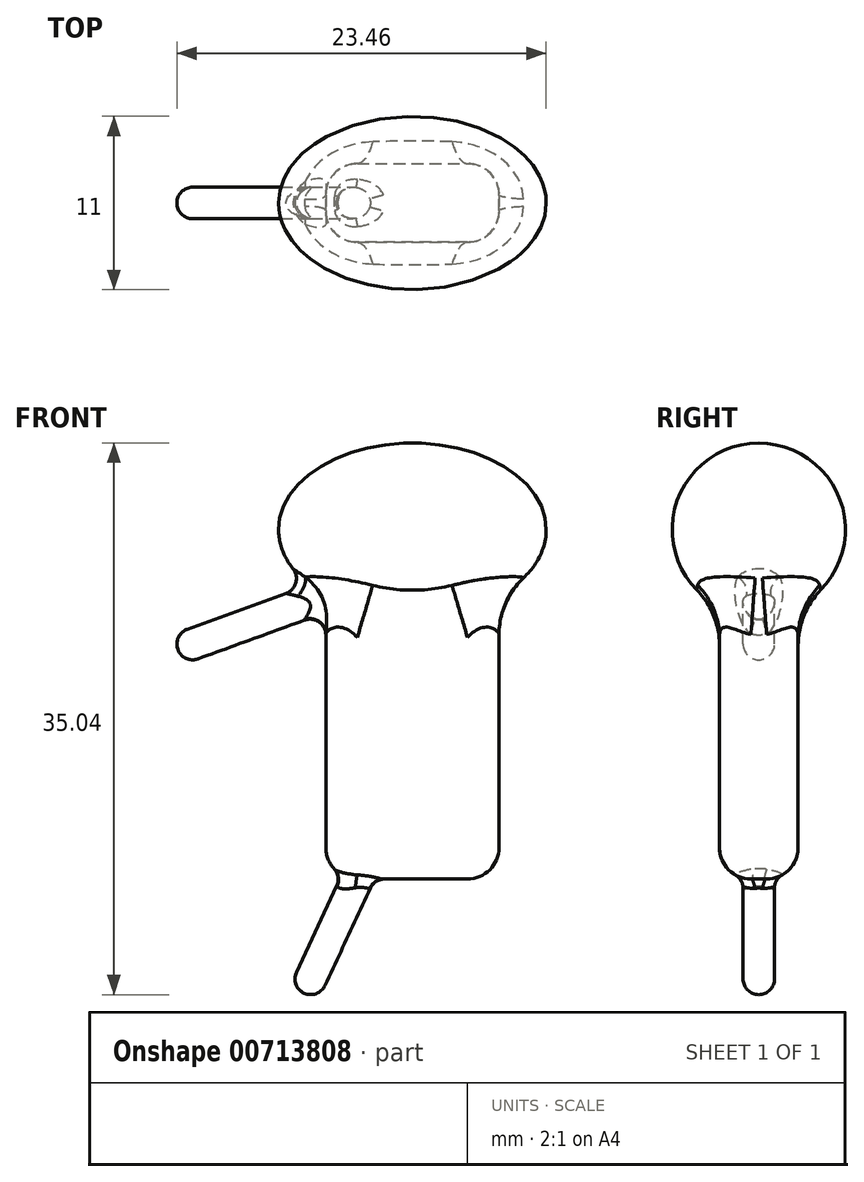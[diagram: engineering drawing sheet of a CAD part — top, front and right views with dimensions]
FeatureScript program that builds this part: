
annotation { "Feature Type Name" : "Feature", "Feature Type Description" : "" }
export const myFeature = defineFeature(function(context is Context, id is Id, definition is map)
    precondition{}
    {
        {
            var Q0;
            Q0=qCreatedBy(makeId("Front.planeOp"),FACE);
            var sketch = newSketch(context, id + "F0", { "sketchPlane" : qUnion([Q0])});
            skLineSegment(sketch, "E0", {"start": v(-29.63, 35) * mm, "end": v(21.78, 35) * mm, "construction": true});
            skEllipse(sketch, "E1", {"center": v(0, 29.5) * mm, "majorRadius": 8.5 * mm, "minorRadius": 5.5 * mm, "majorAxis": v(1, 0)});
            skLineSegment(sketch, "E2.bottom", {"start": v(-5.5, 7.3) * mm, "end": v(5.5, 7.3) * mm});
            skLineSegment(sketch, "E2.top", {"start": v(-5.5, 25.3) * mm, "end": v(5.5, 25.3) * mm});
            skLineSegment(sketch, "E2.left", {"start": v(-5.5, 7.3) * mm, "end": v(-5.5, 25.3) * mm});
            skLineSegment(sketch, "E2.right", {"start": v(5.5, 7.3) * mm, "end": v(5.5, 25.3) * mm});
            skLineSegment(sketch, "E3", {"start": v(-5.5, 25.3) * mm, "end": v(-14.9, 21.89) * mm});
            skLineSegment(sketch, "E4", {"start": v(-3.5, 7.3) * mm, "end": v(-6.9, 0) * mm});
            skLineSegment(sketch, "E5.MirrorCS", {"start": v(5.5, 25.3) * mm, "end": v(14.9, 21.89) * mm});
            skLineSegment(sketch, "E6.MirrorCS", {"start": v(3.5, 7.3) * mm, "end": v(6.9, 0) * mm});
            skLineSegment(sketch, "E7", {"start": v(-8.5, 29.5) * mm, "end": v(8.5, 29.5) * mm});
            skSolve(sketch);
        }
        {
            var Q0;
            {var subQ0=sQuery(id+"F0.wireOp",EDGE,"E7");Q0=makeQuery(id+"F0.imprint","IMPRINT",FACE,{"disambiguationData":[TD([[makeQuery(id+"F0.imprint","IMPRINT",EDGE,{"derivedFrom":subQ0}),1.0]])]});}
            var Q1;
            Q1=sQuery(id+"F0.wireOp",EDGE,"E7");
            revolve(context, id + "F1", {"surfaceOperationType" : NewSurfaceOperationType.NEW, "entities" : qUnion([Q0]), "axis" : qUnion([Q1]), "revolveType" : RevolveType.FULL});
        }
        {
            var Q0;
            {var subQ4=sQuery(id+"F0.wireOp",EDGE,"E2.left");Q0=makeQuery(id+"F0.imprint","IMPRINT",FACE,{"disambiguationData":[TD([[makeQuery(id+"F0.imprint","IMPRINT",EDGE,{"derivedFrom":subQ4}),-1.0]])]});}
            var Q1;
            {var subQ0=sQuery(id+"F0.wireOp",EDGE,"E2.top");Q1=makeQuery(id+"F0.imprint","IMPRINT",FACE,{"disambiguationData":[TD([[makeQuery(id+"F0.imprint","IMPRINT",EDGE,{"derivedFrom":subQ0}),-1.0]])]});}
            extrude(context, id + "F2", {"entities" : qUnion([Q0, Q1]), "operationType" : NewBodyOperationType.ADD, "endBound" : BoundingType.SYMMETRIC, "depth" : 5 * mm, "offsetDistance" : 25 * mm});
        }
        {
            var Q0;
            Q0=makeQuery(id+"F2.opExtrude","CAP_EDGE",EDGE,{"disambiguationData":[OSD([sQuery(id+"F0.wireOp",EDGE,"E2.left")])],"isStart":false});
            var Q1;
            Q1=makeQuery(id+"F2.opExtrude","CAP_EDGE",EDGE,{"disambiguationData":[OSD([sQuery(id+"F0.wireOp",EDGE,"E2.left")])],"isStart":true});
            var Q2;
            Q2=makeQuery(id+"F2.opExtrude","CAP_EDGE",EDGE,{"disambiguationData":[OSD([sQuery(id+"F0.wireOp",EDGE,"E2.right")])],"isStart":false});
            var Q3;
            Q3=makeQuery(id+"F2.opExtrude","CAP_EDGE",EDGE,{"disambiguationData":[OSD([sQuery(id+"F0.wireOp",EDGE,"E2.right")])],"isStart":true});
            fillet(context, id + "F3", {"entities" : qUnion([Q0, Q1, Q2, Q3]), "radius" : 2 * mm, "tangentPropagation" : true, "allowEdgeOverflow" : false});
        }
        {
            var Q0;
            Q0=makeQuery(id+"F2.boolean.opBoolean","INTERSECT",EDGE,{"disambiguationData":[OD(1.0)],"derivedFrom":[makeQuery(id+"F1.opRevolve","SWEPT_FACE",FACE,{"disambiguationData":[OSD([sQuery(id+"F0.wireOp",EDGE,"E1")])]}),makeQuery(id+"F2.opExtrude","SWEPT_FACE",FACE,{"disambiguationData":[OSD([sQuery(id+"F0.wireOp",EDGE,"E2.top")])]})]});
            var Q1;
            Q1=makeQuery(id+"F2.boolean.opBoolean","INTERSECT",EDGE,{"derivedFrom":[makeQuery(id+"F1.opRevolve","SWEPT_FACE",FACE,{"disambiguationData":[OSD([sQuery(id+"F0.wireOp",EDGE,"E1")])]}),makeQuery(id+"F2.opExtrude","CAP_FACE",FACE,{"disambiguationData":[OSD([sQuery(id+"F0.wireOp",EDGE,"E2.bottom"),sQuery(id+"F0.wireOp",EDGE,"E2.top"),sQuery(id+"F0.wireOp",EDGE,"E2.left"),sQuery(id+"F0.wireOp",EDGE,"E2.right")])],"isStart":false})]});
            var Q2;
            Q2=makeQuery(id+"F3.opFillet","BLEND_EDGE",EDGE,{"blendedFrom":[makeQuery(id+"F2.opExtrude","CAP_EDGE",EDGE,{"disambiguationData":[OSD([sQuery(id+"F0.wireOp",EDGE,"E2.left")])],"isStart":false}),makeQuery(id+"F1.opRevolve","SWEPT_FACE",FACE,{"disambiguationData":[OSD([sQuery(id+"F0.wireOp",EDGE,"E1")])]})],"blendedInto":[makeQuery(id+"F1.opRevolve","SWEPT_FACE",FACE,{"disambiguationData":[OSD([sQuery(id+"F0.wireOp",EDGE,"E1")])]})]});
            var Q3;
            Q3=makeQuery(id+"F3.opFillet","BLEND_EDGE",EDGE,{"blendedFrom":[makeQuery(id+"F2.opExtrude","CAP_EDGE",EDGE,{"disambiguationData":[OSD([sQuery(id+"F0.wireOp",EDGE,"E2.right")])],"isStart":false}),makeQuery(id+"F1.opRevolve","SWEPT_FACE",FACE,{"disambiguationData":[OSD([sQuery(id+"F0.wireOp",EDGE,"E1")])]})],"blendedInto":[makeQuery(id+"F1.opRevolve","SWEPT_FACE",FACE,{"disambiguationData":[OSD([sQuery(id+"F0.wireOp",EDGE,"E1")])]})]});
            var Q4;
            Q4=makeQuery(id+"F2.boolean.opBoolean","INTERSECT",EDGE,{"disambiguationData":[OD(3.0)],"derivedFrom":[makeQuery(id+"F1.opRevolve","SWEPT_FACE",FACE,{"disambiguationData":[OSD([sQuery(id+"F0.wireOp",EDGE,"E1")])]}),makeQuery(id+"F2.opExtrude","SWEPT_FACE",FACE,{"disambiguationData":[OSD([sQuery(id+"F0.wireOp",EDGE,"E2.top")])]})]});
            var Q5;
            Q5=makeQuery(id+"F2.boolean.opBoolean","INTERSECT",EDGE,{"disambiguationData":[OD(2.0)],"derivedFrom":[makeQuery(id+"F1.opRevolve","SWEPT_FACE",FACE,{"disambiguationData":[OSD([sQuery(id+"F0.wireOp",EDGE,"E1")])]}),makeQuery(id+"F2.opExtrude","SWEPT_FACE",FACE,{"disambiguationData":[OSD([sQuery(id+"F0.wireOp",EDGE,"E2.top")])]})]});
            var Q6;
            Q6=makeQuery(id+"F3.opFillet","BLEND_EDGE",EDGE,{"blendedFrom":[makeQuery(id+"F2.opExtrude","CAP_EDGE",EDGE,{"disambiguationData":[OSD([sQuery(id+"F0.wireOp",EDGE,"E2.right")])],"isStart":true}),makeQuery(id+"F1.opRevolve","SWEPT_FACE",FACE,{"disambiguationData":[OSD([sQuery(id+"F0.wireOp",EDGE,"E1")])]})],"blendedInto":[makeQuery(id+"F1.opRevolve","SWEPT_FACE",FACE,{"disambiguationData":[OSD([sQuery(id+"F0.wireOp",EDGE,"E1")])]})]});
            var Q7;
            Q7=makeQuery(id+"F2.boolean.opBoolean","INTERSECT",EDGE,{"derivedFrom":[makeQuery(id+"F1.opRevolve","SWEPT_FACE",FACE,{"disambiguationData":[OSD([sQuery(id+"F0.wireOp",EDGE,"E1")])]}),makeQuery(id+"F2.opExtrude","CAP_FACE",FACE,{"disambiguationData":[OSD([sQuery(id+"F0.wireOp",EDGE,"E2.bottom"),sQuery(id+"F0.wireOp",EDGE,"E2.top"),sQuery(id+"F0.wireOp",EDGE,"E2.left"),sQuery(id+"F0.wireOp",EDGE,"E2.right")])],"isStart":true})]});
            fillet(context, id + "F4", {"entities" : qUnion([Q0, Q1, Q2, Q3, Q4, Q5, Q6, Q7]), "radius" : 5 * mm, "tangentPropagation" : true, "allowEdgeOverflow" : false});
        }
        {
            var Q0;
            Q0=makeQuery(id+"F2.opExtrude","CAP_EDGE",EDGE,{"disambiguationData":[OSD([sQuery(id+"F0.wireOp",EDGE,"E2.bottom")])],"isStart":true});
            var Q1;
            Q1=makeQuery(id+"F3.opFillet","BLEND_EDGE",EDGE,{"blendedFrom":[makeQuery(id+"F2.opExtrude","CAP_EDGE",EDGE,{"disambiguationData":[OSD([sQuery(id+"F0.wireOp",EDGE,"E2.right")])],"isStart":true}),makeQuery(id+"F2.opExtrude","SWEPT_FACE",FACE,{"disambiguationData":[OSD([sQuery(id+"F0.wireOp",EDGE,"E2.bottom")])]})],"blendedInto":[makeQuery(id+"F2.opExtrude","SWEPT_FACE",FACE,{"disambiguationData":[OSD([sQuery(id+"F0.wireOp",EDGE,"E2.bottom")])]})]});
            var Q2;
            Q2=makeQuery(id+"F2.opExtrude","SWEPT_EDGE",EDGE,{"disambiguationData":[OSD([sQuery(id+"F0.wireOp",EDGE,"E2.bottom"),sQuery(id+"F0.wireOp",EDGE,"E2.right")])]});
            var Q3;
            Q3=makeQuery(id+"F3.opFillet","BLEND_EDGE",EDGE,{"blendedFrom":[makeQuery(id+"F2.opExtrude","CAP_EDGE",EDGE,{"disambiguationData":[OSD([sQuery(id+"F0.wireOp",EDGE,"E2.right")])],"isStart":false}),makeQuery(id+"F2.opExtrude","SWEPT_FACE",FACE,{"disambiguationData":[OSD([sQuery(id+"F0.wireOp",EDGE,"E2.bottom")])]})],"blendedInto":[makeQuery(id+"F2.opExtrude","SWEPT_FACE",FACE,{"disambiguationData":[OSD([sQuery(id+"F0.wireOp",EDGE,"E2.bottom")])]})]});
            var Q4;
            Q4=makeQuery(id+"F2.opExtrude","CAP_EDGE",EDGE,{"disambiguationData":[OSD([sQuery(id+"F0.wireOp",EDGE,"E2.bottom")])],"isStart":false});
            var Q5;
            Q5=makeQuery(id+"F3.opFillet","BLEND_EDGE",EDGE,{"blendedFrom":[makeQuery(id+"F2.opExtrude","CAP_EDGE",EDGE,{"disambiguationData":[OSD([sQuery(id+"F0.wireOp",EDGE,"E2.left")])],"isStart":false}),makeQuery(id+"F2.opExtrude","SWEPT_FACE",FACE,{"disambiguationData":[OSD([sQuery(id+"F0.wireOp",EDGE,"E2.bottom")])]})],"blendedInto":[makeQuery(id+"F2.opExtrude","SWEPT_FACE",FACE,{"disambiguationData":[OSD([sQuery(id+"F0.wireOp",EDGE,"E2.bottom")])]})]});
            var Q6;
            Q6=makeQuery(id+"F2.opExtrude","SWEPT_EDGE",EDGE,{"disambiguationData":[OSD([sQuery(id+"F0.wireOp",EDGE,"E2.bottom"),sQuery(id+"F0.wireOp",EDGE,"E2.left")])]});
            var Q7;
            Q7=makeQuery(id+"F3.opFillet","BLEND_EDGE",EDGE,{"blendedFrom":[makeQuery(id+"F2.opExtrude","CAP_EDGE",EDGE,{"disambiguationData":[OSD([sQuery(id+"F0.wireOp",EDGE,"E2.left")])],"isStart":true}),makeQuery(id+"F2.opExtrude","SWEPT_FACE",FACE,{"disambiguationData":[OSD([sQuery(id+"F0.wireOp",EDGE,"E2.bottom")])]})],"blendedInto":[makeQuery(id+"F2.opExtrude","SWEPT_FACE",FACE,{"disambiguationData":[OSD([sQuery(id+"F0.wireOp",EDGE,"E2.bottom")])]})]});
            fillet(context, id + "F5", {"entities" : qUnion([Q0, Q1, Q2, Q3, Q4, Q5, Q6, Q7]), "radius" : 2 * mm, "tangentPropagation" : true, "allowEdgeOverflow" : false});
        }
        {
            var Q0;
            Q0=sQuery(id+"F0.wireOp",VERTEX,"E3.start");
            var Q1;
            Q1=sQuery(id+"F0.wireOp",EDGE,"E3");
            cPlane(context, id + "F6", {"entities" : qUnion([Q0, Q1]), "cplaneType" : CPlaneType.LINE_POINT, "offset" : 25 * mm, "width" : 150 * mm, "height" : 150 * mm});
        }
        {
            var Q0;
            Q0=qCreatedBy(id+"F6.planeOp",FACE);
            var sketch = newSketch(context, id + "F7", { "sketchPlane" : qUnion([Q0])});
            skCircle(sketch, "E8", {"center": v(0, 25.66) * mm, "radius": 1 * mm});
            skSolve(sketch);
        }
        {
            var Q0;
            Q0 = qSketchRegion(id + "F7", true);
            extrude(context, id + "F8", {"entities" : qUnion([Q0]), "operationType" : NewBodyOperationType.ADD, "depth" : 10 * mm, "offsetDistance" : 25 * mm});
        }
        {
            var Q0;
            Q0=makeQuery(id+"F8.opExtrude","CAP_EDGE",EDGE,{"disambiguationData":[OSD([sQuery(id+"F7.wireOp",EDGE,"E8")])],"isStart":false});
            fillet(context, id + "F9", {"entities" : qUnion([Q0]), "radius" : 1 * mm, "tangentPropagation" : true, "allowEdgeOverflow" : false});
        }
        {
            var Q0;
            {var subQ0=sQuery(id+"F0.wireOp",EDGE,"E1");var subQ1=sQuery(id+"F0.wireOp",EDGE,"E2.left");Q0=makeQuery(id+"F8.boolean.opBoolean","INTERSECT",EDGE,{"derivedFrom":[makeQuery(id+"F4.opFillet","BLEND_FACE",FACE,{"disambiguationData":[OSD([subQ0,subQ1]),TDD([makeQuery(id+"F3.opFillet","BLEND_EDGE",EDGE,{"blendedFrom":[makeQuery(id+"F2.opExtrude","CAP_EDGE",EDGE,{"disambiguationData":[OSD([subQ1])],"isStart":false}),makeQuery(id+"F1.opRevolve","SWEPT_FACE",FACE,{"disambiguationData":[OSD([subQ0])]})],"blendedInto":[makeQuery(id+"F1.opRevolve","SWEPT_FACE",FACE,{"disambiguationData":[OSD([subQ0])]})]})]),OD(1.0)]}),makeQuery(id+"F8.opExtrude","SWEPT_FACE",FACE,{"disambiguationData":[OSD([sQuery(id+"F7.wireOp",EDGE,"E8")])]})]});}
            fillet(context, id + "F10", {"entities" : qUnion([Q0]), "radius" : 1 * mm, "tangentPropagation" : true, "allowEdgeOverflow" : false});
        }
        {
            var Q0;
            Q0=sQuery(id+"F0.wireOp",VERTEX,"E4.start");
            var Q1;
            Q1=sQuery(id+"F0.wireOp",EDGE,"E4");
            cPlane(context, id + "F11", {"entities" : qUnion([Q0, Q1]), "cplaneType" : CPlaneType.LINE_POINT, "offset" : 25 * mm, "width" : 150 * mm, "height" : 150 * mm});
        }
        {
            var Q0;
            Q0=qCreatedBy(id+"F11.planeOp",FACE);
            var sketch = newSketch(context, id + "F12", { "sketchPlane" : qUnion([Q0])});
            skCircle(sketch, "E9", {"center": v(-6.26, 0) * mm, "radius": 1 * mm});
            skSolve(sketch);
        }
        {
            var Q0;
            Q0 = qSketchRegion(id + "F12", true);
            extrude(context, id + "F13", {"entities" : qUnion([Q0]), "operationType" : NewBodyOperationType.ADD, "endBound" : BoundingType.SYMMETRIC, "depth" : 16 * mm, "offsetDistance" : 25 * mm});
        }
        {
            var Q0;
            Q0=makeQuery(id+"F13.opExtrude","CAP_EDGE",EDGE,{"disambiguationData":[OSD([sQuery(id+"F12.wireOp",EDGE,"E9")])],"isStart":false});
            var Q1;
            {var subQ0=sQuery(id+"F0.wireOp",EDGE,"E2.bottom");var subQ1=sQuery(id+"F0.wireOp",EDGE,"E2.left");Q1=makeQuery(id+"F13.boolean.opBoolean","INTERSECT",EDGE,{"derivedFrom":[makeQuery(id+"F5.opFillet","BLEND_FACE",FACE,{"disambiguationData":[OSD([subQ0,subQ1]),TDD([makeQuery(id+"F3.opFillet","BLEND_EDGE",EDGE,{"blendedFrom":[makeQuery(id+"F2.opExtrude","CAP_EDGE",EDGE,{"disambiguationData":[OSD([subQ1])],"isStart":false}),makeQuery(id+"F2.opExtrude","SWEPT_FACE",FACE,{"disambiguationData":[OSD([subQ0])]})],"blendedInto":[makeQuery(id+"F2.opExtrude","SWEPT_FACE",FACE,{"disambiguationData":[OSD([subQ0])]})]})])]}),makeQuery(id+"F13.opExtrude","SWEPT_FACE",FACE,{"disambiguationData":[OSD([sQuery(id+"F12.wireOp",EDGE,"E9")])]})]});}
            fillet(context, id + "F14", {"entities" : qUnion([Q0, Q1]), "radius" : 1 * mm, "tangentPropagation" : true, "allowEdgeOverflow" : false});
        }
    });
